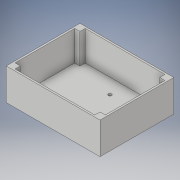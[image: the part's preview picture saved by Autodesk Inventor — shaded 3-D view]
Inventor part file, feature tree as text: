
AUTODESK INVENTOR PART (.ipt)
format: ipt  version: 2018 (Build 220112000, 112)  size: 131,072 bytes
history: native  units: in
note: dims shown in document units (in); Inventor stores cm internally (conversion verified against a paired STEP export)
features: extrude x3, sketch x3
ambient origin geometry x8: Origin, YZ Plane, XZ Plane, XY Plane, X Axis, Y Axis, Z Axis, Center Point
bodies: Solid1 (feature_tree)
feature tree (6):
  extrude  "Extrusion1"  Depth=3.701in
  extrude  "Extrusion2"  Depth=4.527in
  extrude  "Extrusion3"  Depth=0.354in
  sketch  "Sketch1"  dims[d0=4.705in d1=3.701in]
  sketch  "Sketch2"  dims[d2=0.089in d3=0.0in d4=4.527in]
  sketch  "Sketch3"  dims[d5=3.523in d6=0.354in d7=0.354in d10=0.354in d11=0.354in d14=1.5in d15=0.0in d18=0.164in d19=0.164in d20=0.0in d21=0.0in]
